# Revit family: 221017KCG01-011_KMCS122PPS
name_source: partatom
category: Specialty Equipment
units: mm (PartAtom-declared; Revit-internal decimal feet)

## family parameters
Always vertical = Yes
Cut with Voids When Loaded = No
Enable Cutting in Views = No
Maintain Annotation Orientation = No
Part Type = Normal
Room Calculation Point = No
Round Connector Dimension = Use Diameter
Shared = No
Work Plane-Based = No

## types (1)
- KMCS122PPS
    Accent Material = ARCAT - Plastic - Black Light
    Amps = 0 A
    Back Panel Material = ARCAT - Metal - Aluminum
    Body Material = ARCAT - Metal - Steel - Black
    Clearance Material = ARCAT - Clearance
    Default Elevation = 0 "
    Depth = 18.31 "
    Description = KitchenAid® 1.6 Cu. Ft. Countertop Microwave with Auto Functions
    Display Panel Material = ARCAT - Plastic - Gray
    Door Age = ARCAT - Metal - Steel - Aluminium
    Door Frame = ARCAT - Metal - Steel - Gray
    Door Glass = ARCAT - Glass - Tempered - Dark Gray
    Door Material = ARCAT - Metal - Steel - Gray
    Family Name = Countertop Microwave
    Feature 1 = Auto Functions
    Feature 2 = Steam Clean Function
    Feature 3 = 1.6 Cu. Ft. Capacity
    Glass Material = ARCAT - Glass - Tempered - Dark Black
    Handle Material = ARCAT - Metal - Steel - Gray - Dark
    Height = 12.25 "
    Leg Material = ARCAT - Plastic - White
    Logo Material = Stainless Steel
    Voltage = 0 V
    Width = 21.75 "

## geometry (parser evidence)
native form markers: Sweep x31
no freeform markers — native parametric forms only
